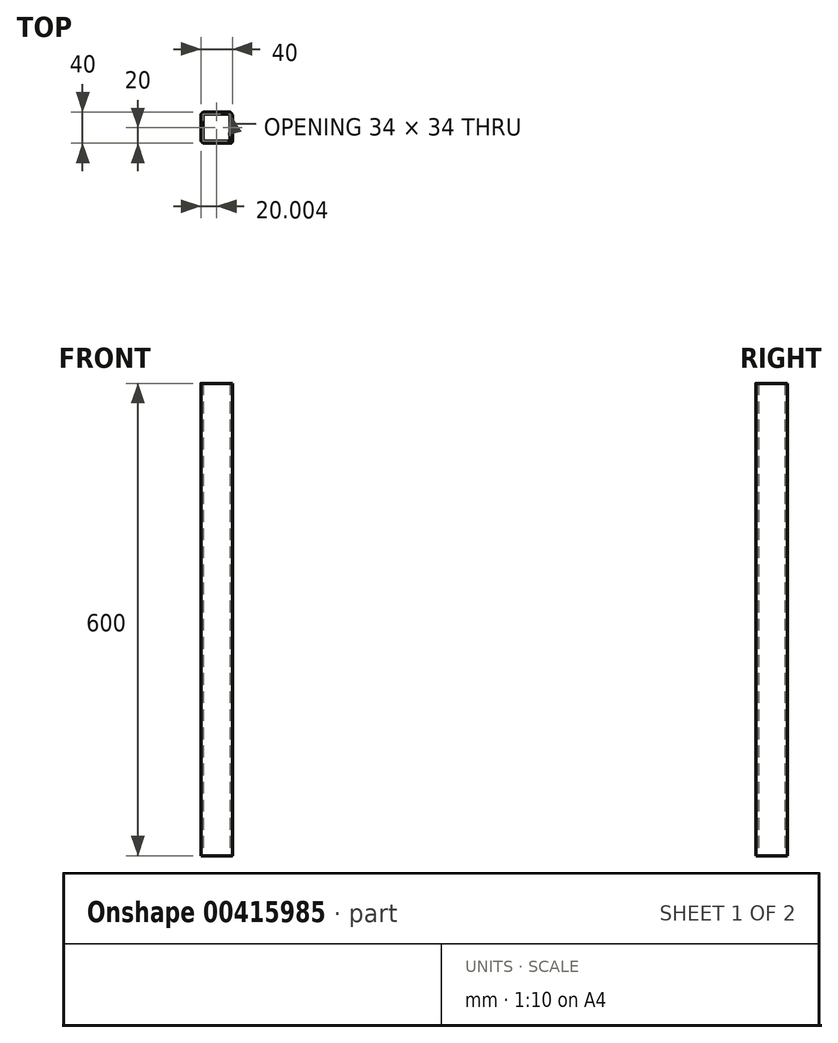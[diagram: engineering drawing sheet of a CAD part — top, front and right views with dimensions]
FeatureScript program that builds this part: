
annotation { "Feature Type Name" : "Feature", "Feature Type Description" : "" }
export const myFeature = defineFeature(function(context is Context, id is Id, definition is map)
    precondition{}
    {
        {
            var Q0;
            Q0=qCreatedBy(makeId("Top.planeOp"),FACE);
            var sketch = newSketch(context, id + "F0", { "sketchPlane" : qUnion([Q0])});
            skLineSegment(sketch, "E0.bottom", {"start": v(17.45, 20) * mm, "end": v(-12.55, 20) * mm});
            skLineSegment(sketch, "E0.top", {"start": v(19.45, -20) * mm, "end": v(-12.55, -20) * mm});
            skLineSegment(sketch, "E0.left", {"start": v(22.45, 15) * mm, "end": v(22.45, -17) * mm});
            skLineSegment(sketch, "E0.right", {"start": v(-17.55, 15) * mm, "end": v(-17.55, -15) * mm});
            skPoint(sketch, "E0.middle", {"position": v(2.45, 0) * mm});
            skPoint(sketch, "E1.visualSharp", {"position": v(22.45, 20) * mm});
            skArc(sketch, "E1.filletArc", {"start": v(22.45, 15) * mm, "mid": v(20.99, 18.54) * mm, "end": v(17.45, 20) * mm});
            skPoint(sketch, "E2.visualSharp", {"position": v(22.45, -20) * mm});
            skArc(sketch, "E2.filletArc", {"start": v(19.45, -20) * mm, "mid": v(21.58, -19.12) * mm, "end": v(22.45, -17) * mm});
            skPoint(sketch, "E3.visualSharp", {"position": v(-17.55, -20) * mm});
            skArc(sketch, "E3.filletArc", {"start": v(-17.55, -15) * mm, "mid": v(-16.08, -18.54) * mm, "end": v(-12.55, -20) * mm});
            skPoint(sketch, "E4.visualSharp", {"position": v(-17.55, 20) * mm});
            skArc(sketch, "E4.filletArc", {"start": v(-12.55, 20) * mm, "mid": v(-16.08, 18.54) * mm, "end": v(-17.55, 15) * mm});
            skLineSegment(sketch, "E5.0", {"start": v(17.45, 17) * mm, "end": v(-12.55, 17) * mm});
            skArc(sketch, "E6.0", {"start": v(19.45, 15) * mm, "mid": v(18.87, 16.41) * mm, "end": v(17.45, 17) * mm});
            skLineSegment(sketch, "E6.1", {"start": v(19.45, 15) * mm, "end": v(19.45, -17) * mm});
            skLineSegment(sketch, "E6.2", {"start": v(19.45, -17) * mm, "end": v(19.45, -17) * mm});
            skArc(sketch, "E6.3", {"start": v(-12.55, 17) * mm, "mid": v(-13.96, 16.41) * mm, "end": v(-14.55, 15) * mm});
            skLineSegment(sketch, "E6.4", {"start": v(-14.55, 15) * mm, "end": v(-14.55, -15) * mm});
            skArc(sketch, "E6.5", {"start": v(-14.55, -15) * mm, "mid": v(-13.96, -16.41) * mm, "end": v(-12.55, -17) * mm});
            skLineSegment(sketch, "E6.6", {"start": v(19.45, -17) * mm, "end": v(-12.55, -17) * mm});
            skSolve(sketch);
        }
        {
            var Q0;
            Q0 = qSketchRegion(id + "F0", true);
            extrude(context, id + "F1", {"entities" : qUnion([Q0]), "depth" : 600 * mm});
        }
    });
